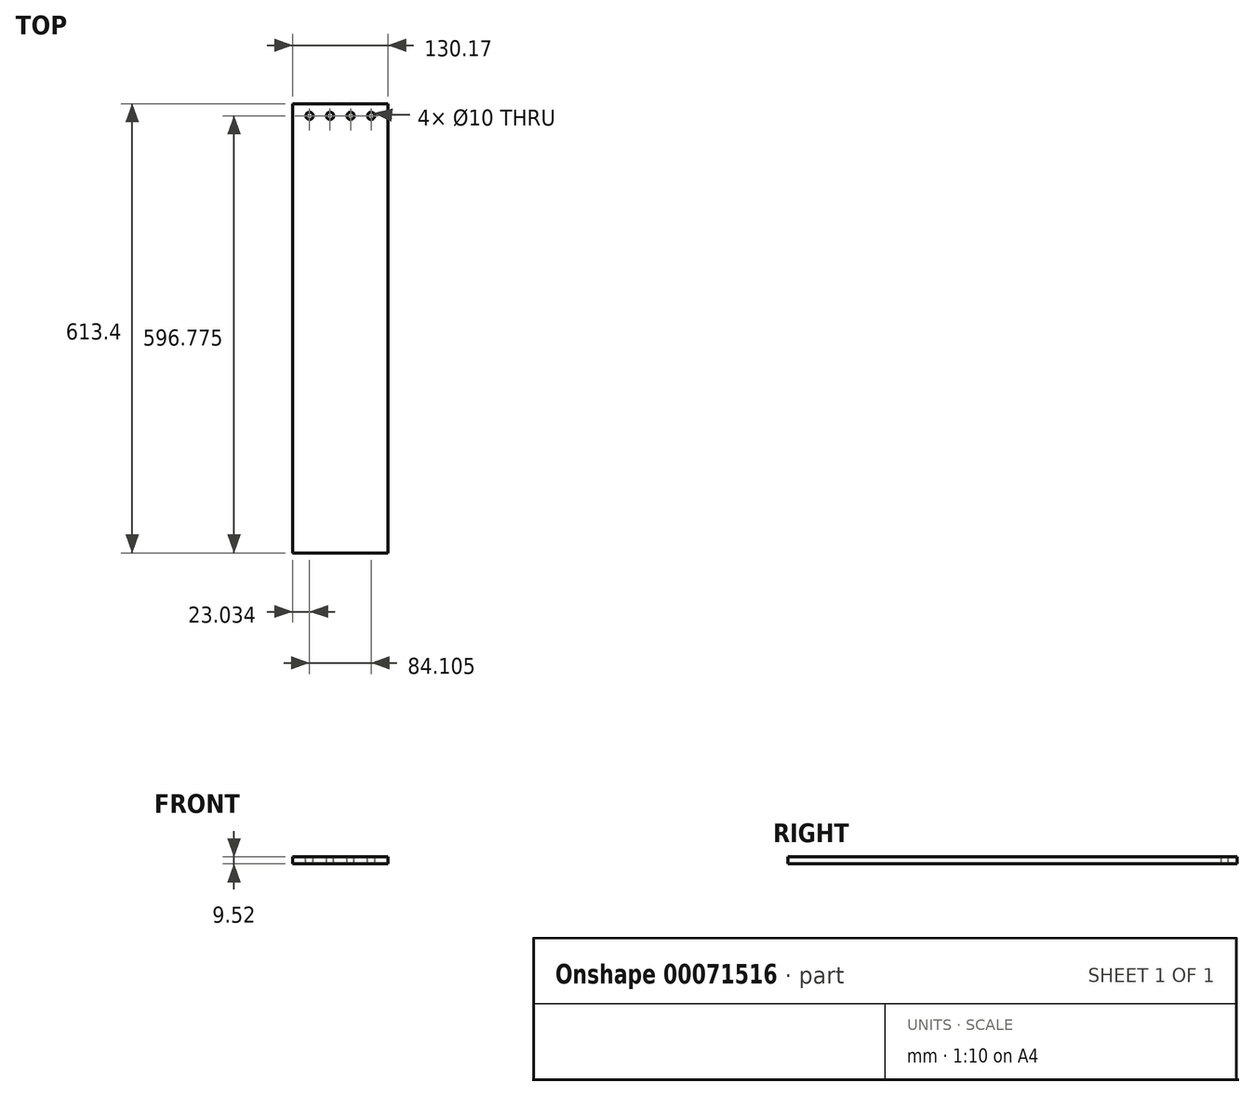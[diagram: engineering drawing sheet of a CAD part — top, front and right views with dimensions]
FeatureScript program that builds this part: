
annotation { "Feature Type Name" : "Feature", "Feature Type Description" : "" }
export const myFeature = defineFeature(function(context is Context, id is Id, definition is map)
    precondition{}
    {
        {
            var Q0;
            Q0=qCreatedBy(makeId("Front.planeOp"),FACE);
            var sketch = newSketch(context, id + "F0", { "sketchPlane" : qUnion([Q0])});
            skLineSegment(sketch, "E0.bottom", {"start": v(-78.85, -15.47) * mm, "end": v(51.32, -15.47) * mm});
            skLineSegment(sketch, "E0.left", {"start": v(-78.85, -15.47) * mm, "end": v(-78.85, -25) * mm});
            skLineSegment(sketch, "E0.right", {"start": v(51.32, -15.47) * mm, "end": v(51.32, -25) * mm});
            skLineSegment(sketch, "E1", {"start": v(-78.85, -25) * mm, "end": v(51.32, -25) * mm});
            skSolve(sketch);
        }
        {
            var Q0;
            Q0=makeQuery(id+"F0.imprint","IMPRINT",FACE,{"disambiguationData":[TD([[makeQuery(id+"F0.imprint","IMPRINT",EDGE,{"derivedFrom":sQuery(id+"F0.wireOp",EDGE,"E0.bottom")}),-1.0]])]});
            extrude(context, id + "F1", {"entities" : qUnion([Q0]), "depth" : 613.4 * mm});
        }
        {
            var Q0;
            Q0=makeQuery(id+"F1.opExtrude","SWEPT_FACE",FACE,{"disambiguationData":[OSD([sQuery(id+"F0.wireOp",EDGE,"E0.bottom")])]});
            var sketch = newSketch(context, id + "F2", { "sketchPlane" : qUnion([Q0])});
            skCircle(sketch, "E2", {"center": v(-55.82, -16.62) * mm, "radius": 5 * mm});
            skCircle(sketch, "E3.1.0.0", {"center": v(-27.78, -16.62) * mm, "radius": 5 * mm});
            skCircle(sketch, "E3.2.0.0", {"center": v(0.25, -16.62) * mm, "radius": 5 * mm});
            skLineSegment(sketch, "E3.direction1", {"start": v(-55.82, -16.62) * mm, "end": v(-27.78, -16.62) * mm, "construction": true});
            skCircle(sketch, "E4.0.3.0", {"center": v(28.29, -16.62) * mm, "radius": 5 * mm});
            skSolve(sketch);
        }
        {
            var Q0;
            Q0 = qSketchRegion(id + "F2", true);
            extrude(context, id + "F3", {"entities" : qUnion([Q0]), "operationType" : NewBodyOperationType.REMOVE, "oppositeDirection" : true, "depth" : 25 * mm});
        }
    });
